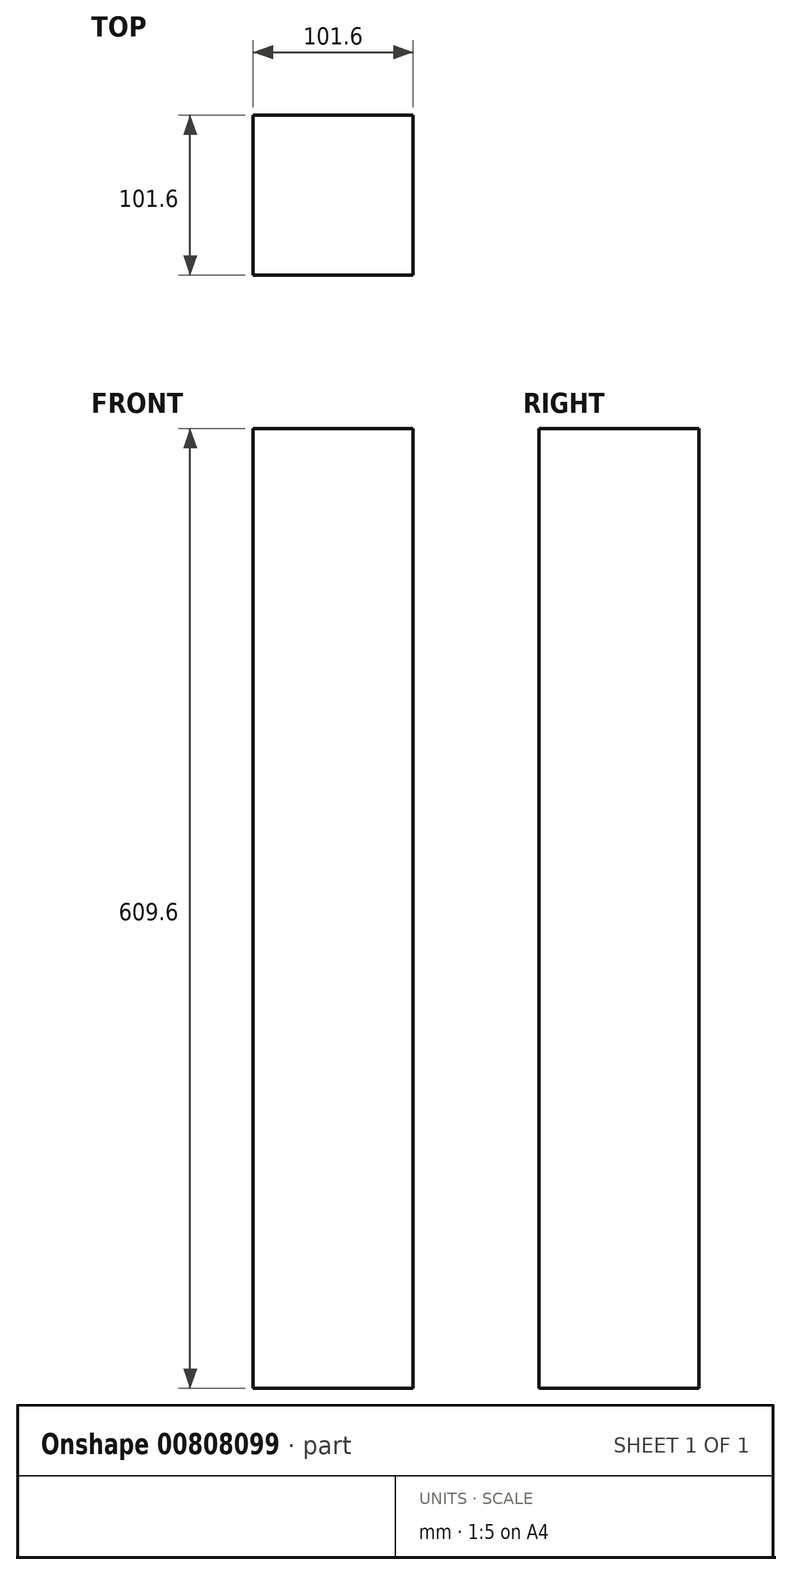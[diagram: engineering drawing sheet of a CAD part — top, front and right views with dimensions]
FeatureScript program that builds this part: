
annotation { "Feature Type Name" : "Feature", "Feature Type Description" : "" }
export const myFeature = defineFeature(function(context is Context, id is Id, definition is map)
    precondition{}
    {
        {
            var Q0;
            Q0=qCreatedBy(makeId("Front.planeOp"),FACE);
            var sketch = newSketch(context, id + "F0", { "sketchPlane" : qUnion([Q0])});
            skLineSegment(sketch, "E0.bottom", {"start": v(50.8, 304.8) * mm, "end": v(-50.8, 304.8) * mm});
            skLineSegment(sketch, "E0.top", {"start": v(50.8, -304.8) * mm, "end": v(-50.8, -304.8) * mm});
            skLineSegment(sketch, "E0.left", {"start": v(50.8, 304.8) * mm, "end": v(50.8, -304.8) * mm});
            skLineSegment(sketch, "E0.right", {"start": v(-50.8, 304.8) * mm, "end": v(-50.8, -304.8) * mm});
            skPoint(sketch, "E0.middle", {"position": v(0, 0) * mm});
            skSolve(sketch);
        }
        {
            var Q0;
            Q0=qSketchRegion(id+"F0",true);
            extrude(context, id + "F1", {"entities" : qUnion([Q0]), "depth" : 101.6 * mm, "offsetDistance" : 25.4 * mm});
        }
    });
